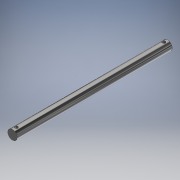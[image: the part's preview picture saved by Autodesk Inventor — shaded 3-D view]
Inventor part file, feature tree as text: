
AUTODESK INVENTOR PART (.ipt)
format: ipt  version: 2017 (Build 210142000, 142)  size: 110,080 bytes
history: native  units: in
note: dims shown in document units (in); Inventor stores cm internally (conversion verified against a paired STEP export)
features: extrude x2, sketch x2
ambient origin geometry x8: Origin, YZ Plane, XZ Plane, XY Plane, X Axis, Y Axis, Z Axis, Center Point
bodies: Solid1 (feature_tree)
feature tree (4):
  extrude  "Extrusion1"  Depth=5.125in TaperAngle=0.0deg
  extrude  "Extrusion2"  Depth=0.104in
  sketch  "Sketch1"  dims[d0=0.3115in d1=5.125in d2=0.0in]
  sketch  "Sketch2"  dims[d3=0.104in d4=0.104in d7=1.0in d8=0.0in d9=0.125in d10=0.125in]
